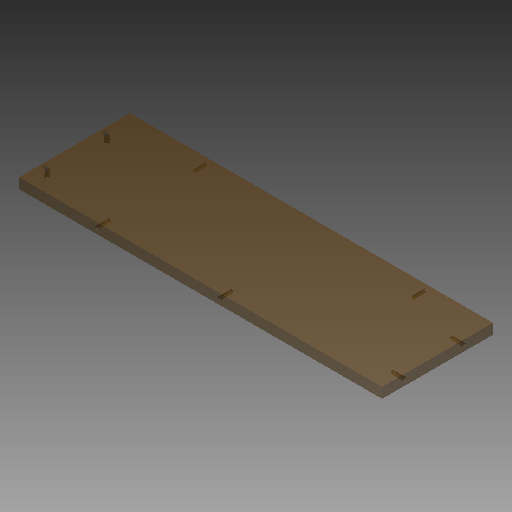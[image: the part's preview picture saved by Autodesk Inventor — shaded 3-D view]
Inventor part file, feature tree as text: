
AUTODESK INVENTOR PART (.ipt)
format: ipt  version: 2018 (Build 220112000, 112)  size: 116,736 bytes
history: native  units: mm
features: hole x4, reference x4, extrude x1
ambient origin geometry x8: Origin, YZ Plane, XZ Plane, XY Plane, X Axis, Y Axis, Z Axis, Center Point
bodies: Volumenkörper1 (feature_tree)
feature tree (9):
  extrude  "Extrusion1"  Depth=281.5mm
  hole  "Bohrung1"  [1 undecoded]
  hole  "Bohrung2"  [1 undecoded]
  hole  "Bohrung3"  [1 undecoded]
  hole  "Bohrung4"  [1 undecoded]
  reference  "Referenz1"
  reference  "Referenz2"
  reference  "Referenz3"
  reference  "Referenz4"
note: 4 required parameter values undecoded (feature->parameter linkage not recoverable at this tier; creation-order binding heuristic only, values carry confidence <= 0.55)
